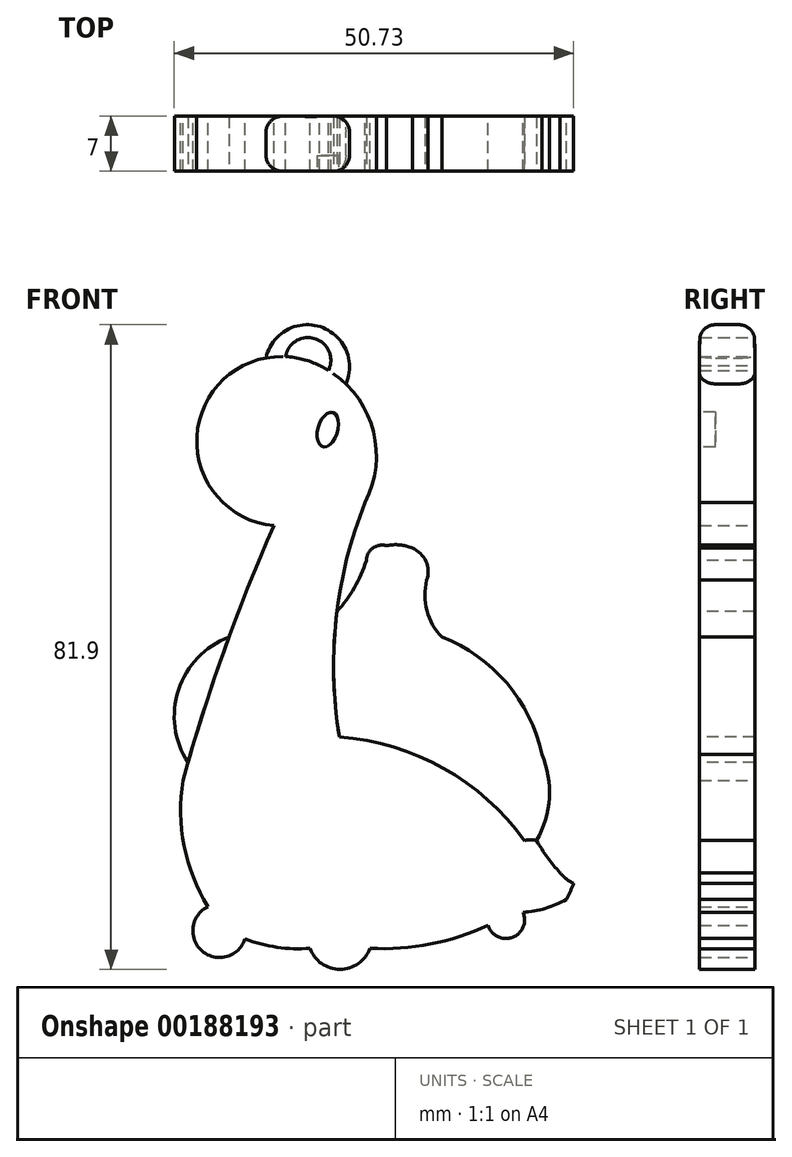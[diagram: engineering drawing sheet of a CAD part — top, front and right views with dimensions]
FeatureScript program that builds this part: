
annotation { "Feature Type Name" : "Feature", "Feature Type Description" : "" }
export const myFeature = defineFeature(function(context is Context, id is Id, definition is map)
    precondition{}
    {
        {
            var Q0;
            Q0=qCreatedBy(makeId("Front.planeOp"),FACE);
            var sketch = newSketch(context, id + "F0", { "sketchPlane" : qUnion([Q0])});
            skArc(sketch, "E0", {"start": v(-9.75, 31.23) * mm, "mid": v(-11.85, 32.02) * mm, "end": v(-14.06, 32.36) * mm});
            skArc(sketch, "E1", {"start": v(-3.96, 13.86) * mm, "mid": v(-2.7, 21.79) * mm, "end": v(-6.42, 28.9) * mm});
            skArc(sketch, "E2", {"start": v(-3.96, 13.86) * mm, "mid": v(-7.78, -2.23) * mm, "end": v(-6.7, -18.74) * mm});
            skArc(sketch, "E3", {"start": v(-15.55, 10.9) * mm, "mid": v(-21.92, -5.08) * mm, "end": v(-27.11, -21.48) * mm});
            skArc(sketch, "E4", {"start": v(-27.11, -21.48) * mm, "mid": v(-26.95, -29.78) * mm, "end": v(-23.94, -37.53) * mm});
            skPoint(sketch, "E4.endSnap0", {"position": v(-21.92, -5.08) * mm});
            skArc(sketch, "E5", {"start": v(-19.23, -41.62) * mm, "mid": v(-15.16, -42.66) * mm, "end": v(-10.97, -42.8) * mm});
            skArc(sketch, "E6", {"start": v(-23.94, -37.53) * mm, "mid": v(-24.69, -43.14) * mm, "end": v(-19.23, -41.62) * mm});
            skArc(sketch, "E7", {"start": v(-10.97, -42.8) * mm, "mid": v(-7.16, -45.48) * mm, "end": v(-3.35, -42.8) * mm});
            skArc(sketch, "E8", {"start": v(-3.35, -42.8) * mm, "mid": v(4.33, -42.26) * mm, "end": v(11.65, -39.87) * mm});
            skArc(sketch, "E9", {"start": v(11.65, -39.87) * mm, "mid": v(14.74, -41.42) * mm, "end": v(16.08, -38.23) * mm});
            skArc(sketch, "E10", {"start": v(16.85, -29.98) * mm, "mid": v(6.44, -20.18) * mm, "end": v(-7.23, -15.97) * mm});
            skArc(sketch, "E11", {"start": v(17.81, -29.11) * mm, "mid": v(17.04, -29.02) * mm, "end": v(16.26, -29.12) * mm});
            skArc(sketch, "E12", {"start": v(17.81, -29.11) * mm, "mid": v(19.19, -31.25) * mm, "end": v(20.81, -33.2) * mm});
            skArc(sketch, "E13", {"start": v(20.81, -33.2) * mm, "mid": v(21.59, -33.99) * mm, "end": v(22.52, -34.57) * mm});
            skArc(sketch, "E14", {"start": v(21.59, -36.58) * mm, "mid": v(22.1, -35.6) * mm, "end": v(22.52, -34.57) * mm});
            skPoint(sketch, "E14.startSnap0", {"position": v(21.59, -33.99) * mm});
            skArc(sketch, "E15", {"start": v(16.08, -38.23) * mm, "mid": v(18.93, -37.73) * mm, "end": v(21.59, -36.58) * mm});
            skPoint(sketch, "E16.orphan", {"position": v(-21.92, -40.37) * mm});
            skArc(sketch, "E17", {"start": v(-6.42, 28.9) * mm, "mid": v(-9.66, 36.16) * mm, "end": v(-16.55, 32.2) * mm});
            skArc(sketch, "E18", {"start": v(-8.63, 30.61) * mm, "mid": v(-10.33, 34.65) * mm, "end": v(-14.06, 32.36) * mm});
            skArc(sketch, "E19.trimOffspring", {"start": v(-16.55, 32.2) * mm, "mid": v(-25.13, 19.43) * mm, "end": v(-12.19, 11.12) * mm});
            skArc(sketch, "E20.trimOffspring", {"start": v(-8.63, 30.61) * mm, "mid": v(-9.18, 30.93) * mm, "end": v(-9.75, 31.23) * mm});
            skSolve(sketch);
        }
        {
            var Q0;
            {var subQ1=sQuery(id+"F0.wireOp",EDGE,"E1");Q0=makeQuery(id+"F0.imprint","IMPRINT",FACE,{"disambiguationData":[TD([[makeQuery(id+"F0.imprint","IMPRINT",EDGE,{"derivedFrom":subQ1}),1.0]])]});}
            extrude(context, id + "F1", {"entities" : qUnion([Q0]), "depth" : 7 * mm});
        }
        {
            var Q0;
            Q0=makeQuery(id+"F1.opExtrude","CAP_FACE",FACE,{"disambiguationData":[OSD([sQuery(id+"F0.wireOp",EDGE,"E0"),sQuery(id+"F0.wireOp",EDGE,"E1"),sQuery(id+"F0.wireOp",EDGE,"E2"),sQuery(id+"F0.wireOp",EDGE,"E3"),sQuery(id+"F0.wireOp",EDGE,"E4"),sQuery(id+"F0.wireOp",EDGE,"E5"),sQuery(id+"F0.wireOp",EDGE,"E6"),sQuery(id+"F0.wireOp",EDGE,"E7"),sQuery(id+"F0.wireOp",EDGE,"E8"),sQuery(id+"F0.wireOp",EDGE,"E9"),sQuery(id+"F0.wireOp",EDGE,"E10"),sQuery(id+"F0.wireOp",EDGE,"E11"),sQuery(id+"F0.wireOp",EDGE,"E12"),sQuery(id+"F0.wireOp",EDGE,"E13"),sQuery(id+"F0.wireOp",EDGE,"E14"),sQuery(id+"F0.wireOp",EDGE,"E15")])],"isStart":false});
            var sketch = newSketch(context, id + "F2", { "sketchPlane" : qUnion([Q0])});
            skArc(sketch, "E21", {"start": v(-21.26, -3.27) * mm, "mid": v(-27.68, -9.97) * mm, "end": v(-26.46, -19.17) * mm});
            skArc(sketch, "E22", {"start": v(-7.54, 0) * mm, "mid": v(-5.33, 3.02) * mm, "end": v(-3.8, 6.44) * mm});
            skArc(sketch, "E23", {"start": v(-1.23, 8.34) * mm, "mid": v(-3, 8.04) * mm, "end": v(-3.8, 6.44) * mm});
            skArc(sketch, "E24", {"start": v(2.03, 8.04) * mm, "mid": v(0.42, 8.44) * mm, "end": v(-1.23, 8.34) * mm});
            skPoint(sketch, "E24.startSnap0", {"position": v(-3, 8.04) * mm});
            skArc(sketch, "E25", {"start": v(3.86, 3.96) * mm, "mid": v(3.75, 6.36) * mm, "end": v(2.03, 8.04) * mm});
            skArc(sketch, "E26", {"start": v(3.86, 3.96) * mm, "mid": v(3.87, 0.1) * mm, "end": v(5.8, -3.27) * mm});
            skArc(sketch, "E27", {"start": v(18.49, -18.16) * mm, "mid": v(14.03, -9.1) * mm, "end": v(5.8, -3.27) * mm});
            skArc(sketch, "E28", {"start": v(17.81, -29.11) * mm, "mid": v(19.44, -23.72) * mm, "end": v(18.49, -18.16) * mm});
            skArc(sketch, "E29", {"start": v(5.8, -3.27) * mm, "mid": v(-0.95, -2.15) * mm, "end": v(-7.79, -2.38) * mm});
            skSolve(sketch);
        }
        {
            var Q0;
            {var subQ0=sQuery(id+"F2.wireOp",EDGE,"E21");Q0=makeQuery(id+"F2.imprint","IMPRINT",FACE,{"disambiguationData":[TD([[makeQuery(id+"F2.imprint","IMPRINT",EDGE,{"derivedFrom":subQ0}),1.0]])]});}
            var Q1;
            Q1=makeQuery(id+"F2.imprint","IMPRINT",FACE,{"disambiguationData":[TD([[makeQuery(id+"F2.imprint","IMPRINT",EDGE,{"derivedFrom":sQuery(id+"F2.wireOp",EDGE,"E27")}),1.0]])]});
            var Q2;
            {var subQ0=sQuery(id+"F2.wireOp",EDGE,"E22");Q2=makeQuery(id+"F2.imprint","IMPRINT",FACE,{"disambiguationData":[TD([[makeQuery(id+"F2.imprint","IMPRINT",EDGE,{"derivedFrom":subQ0}),-1.0]])]});}
            extrude(context, id + "F3", {"entities" : qUnion([Q0, Q1, Q2]), "oppositeDirection" : true, "depth" : 7 * mm});
        }
        {
            var Q0;
            Q0=makeQuery(id+"F1.opExtrude","CAP_FACE",FACE,{"disambiguationData":[OSD([sQuery(id+"F0.wireOp",EDGE,"E0"),sQuery(id+"F0.wireOp",EDGE,"E1"),sQuery(id+"F0.wireOp",EDGE,"E2"),sQuery(id+"F0.wireOp",EDGE,"E3"),sQuery(id+"F0.wireOp",EDGE,"E4"),sQuery(id+"F0.wireOp",EDGE,"E5"),sQuery(id+"F0.wireOp",EDGE,"E6"),sQuery(id+"F0.wireOp",EDGE,"E7"),sQuery(id+"F0.wireOp",EDGE,"E8"),sQuery(id+"F0.wireOp",EDGE,"E9"),sQuery(id+"F0.wireOp",EDGE,"E10"),sQuery(id+"F0.wireOp",EDGE,"E11"),sQuery(id+"F0.wireOp",EDGE,"E12"),sQuery(id+"F0.wireOp",EDGE,"E13"),sQuery(id+"F0.wireOp",EDGE,"E14"),sQuery(id+"F0.wireOp",EDGE,"E15")])],"isStart":false});
            var sketch = newSketch(context, id + "F4", { "sketchPlane" : qUnion([Q0])});
            skEllipse(sketch, "E30", {"center": v(-8.7, 23.1) * mm, "majorRadius": 2.27 * mm, "minorRadius": 1.26 * mm, "majorAxis": v(0.28, 0.96)});
            skSolve(sketch);
        }
        {
            var Q0;
            Q0=makeQuery(id+"F4.imprint","IMPRINT",FACE,{"disambiguationData":[TD([[makeQuery(id+"F4.imprint","IMPRINT",EDGE,{"derivedFrom":sQuery(id+"F4.wireOp",EDGE,"E30")}),1.0]])]});
            extrude(context, id + "F5", {"entities" : qUnion([Q0]), "operationType" : NewBodyOperationType.REMOVE, "oppositeDirection" : true, "depth" : 2 * mm});
        }
        {
            var Q0;
            Q0=makeQuery(id+"F1.opExtrude","CAP_EDGE",EDGE,{"disambiguationData":[OSD([sQuery(id+"F0.wireOp",EDGE,"E17")])],"isStart":false});
            var Q1;
            Q1=makeQuery(id+"F1.opExtrude","CAP_EDGE",EDGE,{"disambiguationData":[OSD([sQuery(id+"F0.wireOp",EDGE,"E17")])],"isStart":true});
            fillet(context, id + "F6", {"entities" : qUnion([Q0, Q1]), "radius" : 2 * mm, "tangentPropagation" : true, "allowEdgeOverflow" : false});
        }
    });
